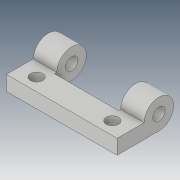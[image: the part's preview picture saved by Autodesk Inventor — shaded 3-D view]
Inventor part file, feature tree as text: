
AUTODESK INVENTOR PART (.ipt)
format: ipt  version: 2019 (Build 230136000, 136)  size: 178,176 bytes
history: native  units: mm
features: extrude x6, sketch x5, plane x5, other x3, move_body x2, fillet x1, direct_edit x1, projected_geometry x1
ambient origin geometry x8: Origin, YZ Plane, XZ Plane, XY Plane, X Axis, Y Axis, Z Axis, Center Point
bodies: Solid1 (feature_tree)
feature tree (24):
  extrude  "Extrusion1"  Depth=45.0mm
  sketch  "Sketch4"  dims[d5=5.0mm d6=5.0mm d7=11.0mm]
  extrude  "Extrusion4"  Depth=5.0mm
  fillet  "Fillet1"  Radius=11.0mm
  extrude  "Extrusion5"  Depth=23.0mm
  plane  "Work Plane1"
  extrude  "Extrusion6"  Depth=12.0mm
  plane  "Work Plane8"
  plane  "Work Plane10"
  sketch  "Sketch11"  dims[d21=0.0mm d24=3.0mm d25=0.0mm d26=12.0mm d27=5.0mm d28=3.0mm d29=0.0mm d33=5.0mm d34=5.0mm d35=17.8mm d36=7.0mm d37=17.8mm d38=7.1mm d39=30.8mm d40=7.1mm d41=3.0mm d42=0.0mm d52=0.0mm d53=0.0mm d54=0.0mm d55=10.0mm d56=0.0mm d57=10.0mm d58=0.0mm d59=0.0mm d60=0.0mm d61=-1.5mm d62=0.0mm d63=0.0mm d64=-1.5mm]
  plane  "Work Plane11"
  plane  "Work Plane12"
  extrude  "Extrusion10"  Depth=10.0mm TaperAngle=0.0deg
  extrude  "Extrusion11"  Depth=12.0mm
  direct_edit  "Direct Edit1"
  sketch  "Sketch1"  dims[d0=6.0mm d1=0.0mm d4=45.0mm]
  sketch  "Sketch5"  dims[d8=11.0mm d9=23.0mm]
  sketch  "Sketch6"  dims[d10=10.0mm d20=12.0mm]
  projected_geometry  "Projected Loop4"
  move_body  "Move1"
  move_body  "Move2"
  parser-record x1  (decoder bookkeeping rows leaked as tree rows — omitted from the tree; the rows remain in map.json)
  other  "Cerniera Assemb.iam"
  other  "Cerniera 1:2"
note: 1 file-system path scrubbed to <path> (originals preserved in map.json)
